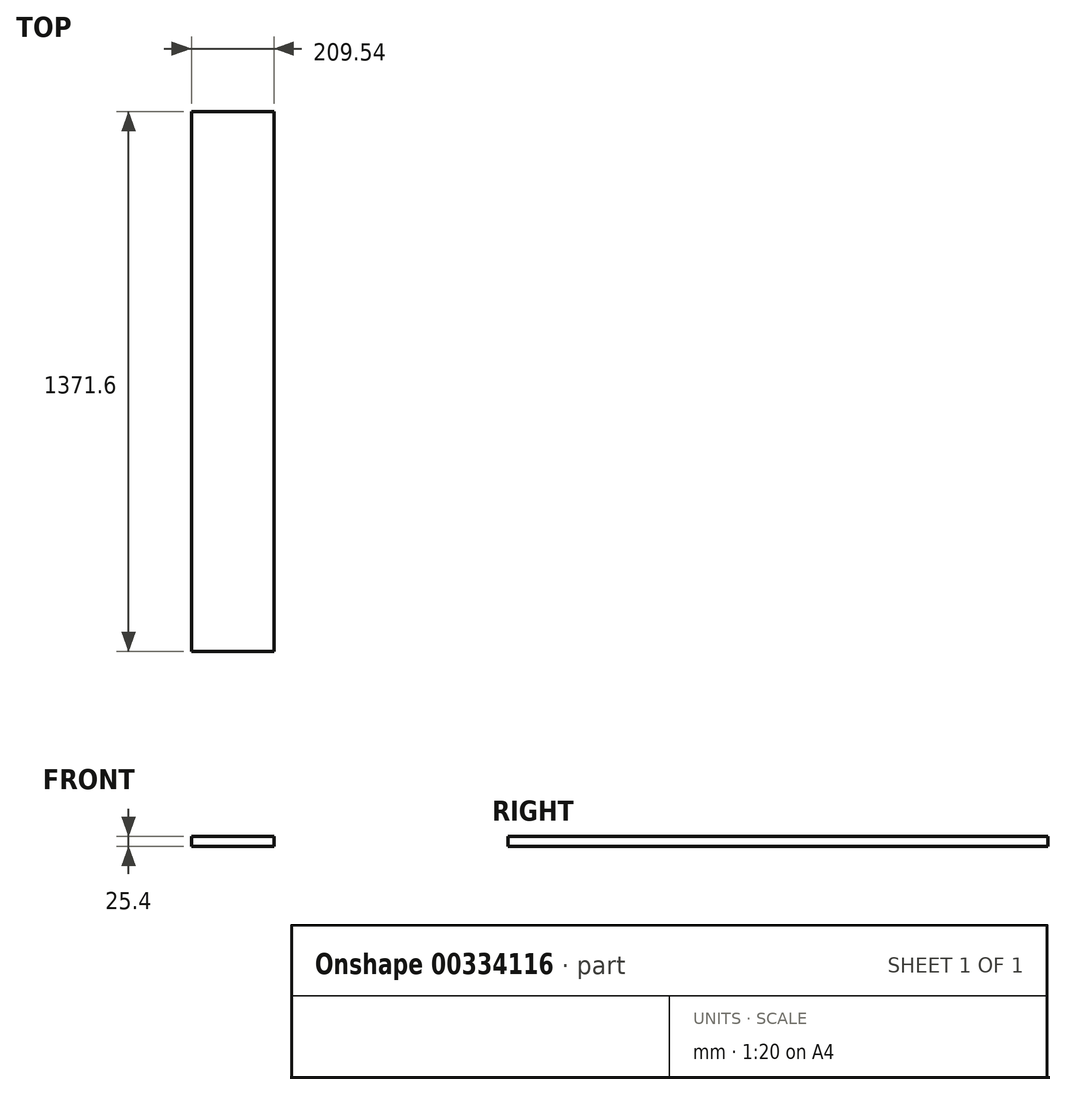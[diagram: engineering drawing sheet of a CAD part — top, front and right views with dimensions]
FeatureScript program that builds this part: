
annotation { "Feature Type Name" : "Feature", "Feature Type Description" : "" }
export const myFeature = defineFeature(function(context is Context, id is Id, definition is map)
    precondition{}
    {
        {
            var Q0;
            Q0=qCreatedBy(makeId("Front.planeOp"),FACE);
            var sketch = newSketch(context, id + "F0", { "sketchPlane" : qUnion([Q0])});
            skLineSegment(sketch, "E0.bottom", {"start": v(104.78, 12.7) * mm, "end": v(-104.78, 12.7) * mm});
            skLineSegment(sketch, "E0.top", {"start": v(104.78, -12.7) * mm, "end": v(-104.78, -12.7) * mm});
            skLineSegment(sketch, "E0.left", {"start": v(104.78, 12.7) * mm, "end": v(104.78, -12.7) * mm});
            skLineSegment(sketch, "E0.right", {"start": v(-104.78, 12.7) * mm, "end": v(-104.78, -12.7) * mm});
            skPoint(sketch, "E0.middle", {"position": v(0, 0) * mm});
            skSolve(sketch);
        }
        {
            var Q0;
            Q0 = qSketchRegion(id + "F0", true);
            extrude(context, id + "F1", {"entities" : qUnion([Q0]), "depth" : 1371.6 * mm, "symmetric" : true});
        }
    });
